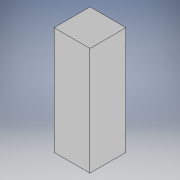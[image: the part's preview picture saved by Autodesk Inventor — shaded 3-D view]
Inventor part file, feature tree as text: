
AUTODESK INVENTOR PART (.ipt)
format: ipt  version: 2018 (Build 220112000, 112)  size: 88,576 bytes
history: native  units: in
note: dims shown in document units (in); Inventor stores cm internally (conversion verified against a paired STEP export)
features: extrude x1, sketch x1
ambient origin geometry x8: Origin, YZ Plane, XZ Plane, XY Plane, X Axis, Y Axis, Z Axis, Center Point
bodies: Solid1 (feature_tree)
feature tree (2):
  extrude  "Extrusion1"  Depth=3.0in
  sketch  "Sketch1"  dims[d0=1.0in d1=3.0in d2=1.0in d3=0.0in]
